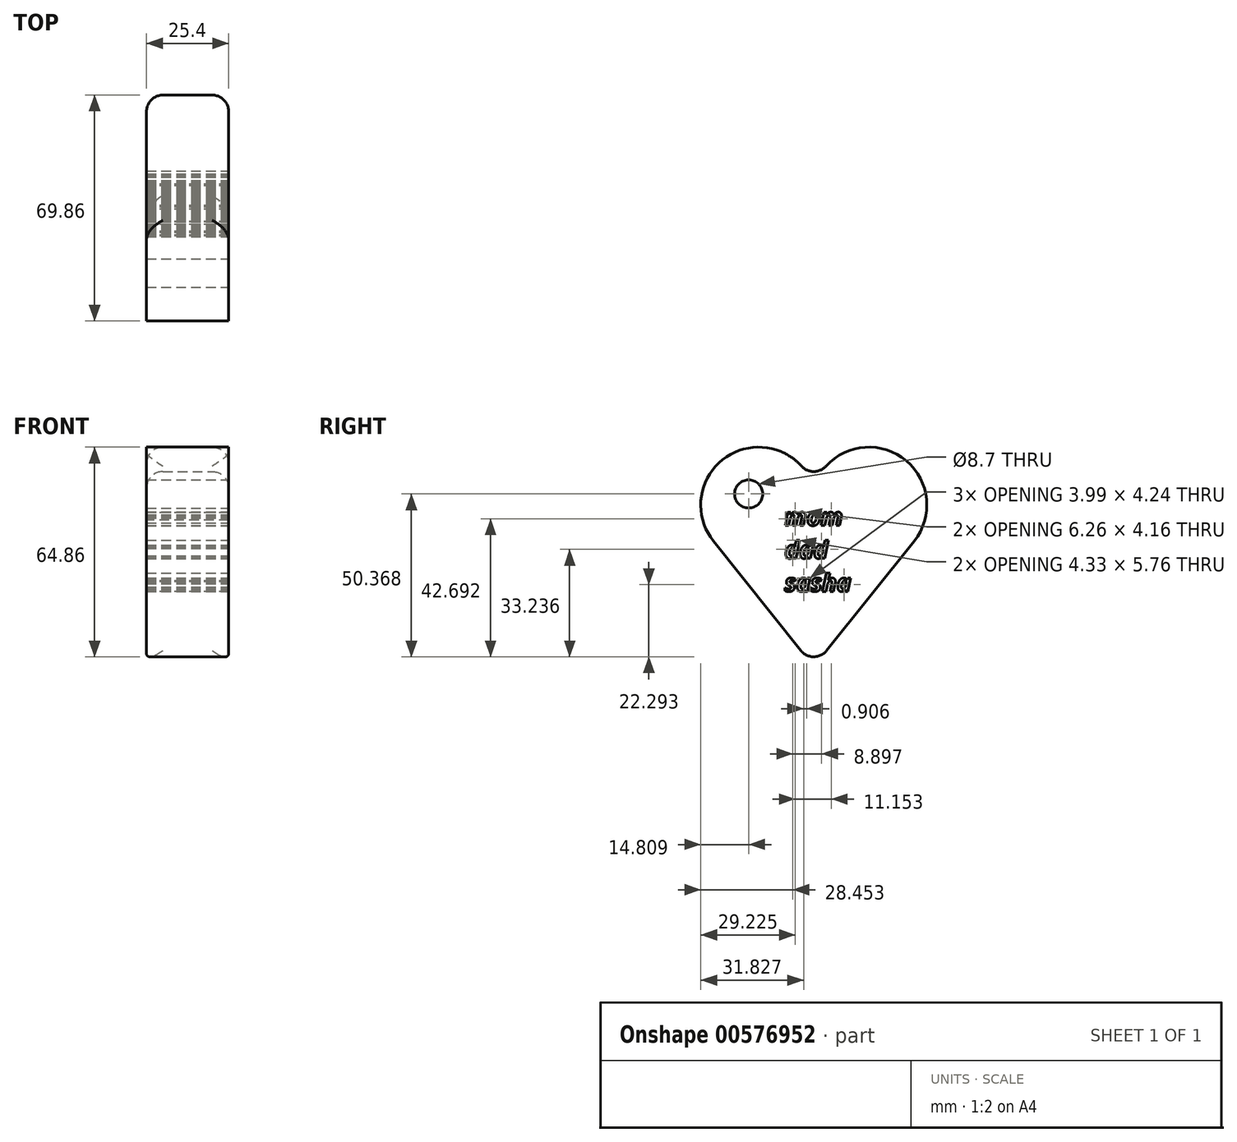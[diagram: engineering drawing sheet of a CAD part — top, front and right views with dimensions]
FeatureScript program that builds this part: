
annotation { "Feature Type Name" : "Feature", "Feature Type Description" : "" }
export const myFeature = defineFeature(function(context is Context, id is Id, definition is map)
    precondition{}
    {
        {
            var Q0;
            Q0=qCreatedBy(makeId("Right.planeOp"),FACE);
            var sketch = newSketch(context, id + "F0", { "sketchPlane" : qUnion([Q0])});
            skLineSegment(sketch, "E0", {"start": v(0, -38.87) * mm, "end": v(31.03, 0) * mm});
            skArc(sketch, "E1", {"start": v(31.03, 0) * mm, "mid": v(25.48, 26.94) * mm, "end": v(0, 16.6) * mm});
            skArc(sketch, "E2.MirrorCS", {"start": v(-31.03, 0) * mm, "mid": v(-25.48, 26.94) * mm, "end": v(0, 16.6) * mm});
            skLineSegment(sketch, "E3.MirrorCS", {"start": v(0, -38.87) * mm, "end": v(-31.03, 0) * mm});
            skSolve(sketch);
        }
        {
            var Q0;
            Q0 = qSketchRegion(id + "F0", true);
            extrude(context, id + "F1", {"entities" : qUnion([Q0]), "depth" : 25.4 * mm, "offsetDistance" : 25.4 * mm});
        }
        {
            var Q0;
            Q0=makeQuery(id+"F1.opExtrude","CAP_FACE",FACE,{"disambiguationData":[OSD([sQuery(id+"F0.wireOp",EDGE,"E0"),sQuery(id+"F0.wireOp",EDGE,"E1"),sQuery(id+"F0.wireOp",EDGE,"E2.MirrorCS"),sQuery(id+"F0.wireOp",EDGE,"E3.MirrorCS")])],"isStart":false});
            var sketch = newSketch(context, id + "F2", { "sketchPlane" : qUnion([Q0])});
            skText(sketch, "E4", { "text": "mom\ndad\nsasha", "fontName": "OpenSans-BoldItalic.ttf"});
            const initialGuessF2  = {"E4": [-0.00897, 0.0048, 1, 0, 0.00539]};
            skSetInitialGuess(sketch, initialGuessF2);
            skSolve(sketch);
        }
        {
            var Q0;
            Q0 = qSketchRegion(id + "F2", true);
            extrude(context, id + "F3", {"entities" : qUnion([Q0]), "operationType" : NewBodyOperationType.REMOVE, "oppositeDirection" : true, "depth" : 152.4 * mm, "offsetDistance" : 25.4 * mm});
        }
        {
            var Q0;
            Q0=makeQuery(id+"F1.opExtrude","SWEPT_FACE",FACE,{"disambiguationData":[OSD([sQuery(id+"F0.wireOp",EDGE,"E1")])]});
            var Q1;
            Q1=makeQuery(id+"F1.opExtrude","SWEPT_EDGE",EDGE,{"disambiguationData":[OSD([sQuery(id+"F0.wireOp",EDGE,"E0"),sQuery(id+"F0.wireOp",EDGE,"E3.MirrorCS")])]});
            fillet(context, id + "F4", {"entities" : qUnion([Q0, Q1]), "radius" : 5.08 * mm, "tangentPropagation" : true, "allowEdgeOverflow" : false});
        }
        {
            var Q0;
            {var subQ0=sQuery(id+"F0.wireOp",EDGE,"E2.MirrorCS");var subQ1=sQuery(id+"F0.wireOp",EDGE,"E0");var subQ2=sQuery(id+"F0.wireOp",EDGE,"E3.MirrorCS");var subQ3=sQuery(id+"F0.wireOp",EDGE,"E1");Q0=makeQuery(id+"F3.boolean.opBoolean","SPLIT",FACE,{"disambiguationData":[TD([makeQuery(id+"F1.opExtrude","SWEPT_FACE",FACE,{"disambiguationData":[OSD([subQ1])]})])],"derivedFrom":makeQuery(id+"F1.opExtrude","CAP_FACE",FACE,{"disambiguationData":[OSD([subQ1,subQ3,subQ0,subQ2])],"isStart":false})});}
            var sketch = newSketch(context, id + "F5", { "sketchPlane" : qUnion([Q0])});
            skCircle(sketch, "E5", {"center": v(-20.12, 14.56) * mm, "radius": 4.35 * mm});
            skSolve(sketch);
        }
        {
            var Q0;
            Q0=makeQuery(id+"F5.imprint","IMPRINT",FACE,{"disambiguationData":[TD([[makeQuery(id+"F5.imprint","IMPRINT",EDGE,{"derivedFrom":sQuery(id+"F5.wireOp",EDGE,"E5")}),1.0]])]});
            extrude(context, id + "F6", {"entities" : qUnion([Q0]), "operationType" : NewBodyOperationType.REMOVE, "oppositeDirection" : true, "depth" : 152.4 * mm, "offsetDistance" : 25.4 * mm});
        }
    });
